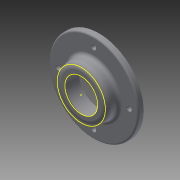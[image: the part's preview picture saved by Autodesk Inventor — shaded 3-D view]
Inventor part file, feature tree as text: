
AUTODESK INVENTOR PART (.ipt)
format: ipt  version: 2014 SP2 (Build 180246200, 246)  size: 164,864 bytes
history: native  units: mm
features: sketch x6, extrude x5, fillet x4, chamfer x1
ambient origin geometry x8: Origin, YZ Plane, XZ Plane, XY Plane, X Axis, Y Axis, Z Axis, Center Point
bodies: Solid1 (feature_tree)
feature tree (16):
  extrude  "Extrusion1"  Depth=28.5mm
  extrude  "Extrusion2"  Depth=13.5mm
  extrude  "Extrusion3"  Depth=3.0mm
  chamfer  "Chamfer2"  Distance=8.0mm
  fillet  "Fillet1"  Radius=50.5mm
  fillet  "Fillet2"  Radius=3.0mm
  fillet  "Fillet3"  Radius=5.0mm
  extrude  "Extrusion4"  Depth=1.0mm
  extrude  "Extrusion5"  Depth=3.0mm
  sketch  "Sketch7"  dims[d21=3.0mm d22=20.0mm d23=3.0mm d24=20.0mm d25=3.0mm d26=20.0mm d27=3.0mm d28=20.0mm d29=11.0mm d30=0.0mm d31=2.5mm d32=0.0mm d33=3.0mm]
  fillet  "Fillet4"  Radius=3.0mm
  sketch  "Sketch1"  dims[d0=22.5mm d1=28.5mm]
  sketch  "Sketch2"  dims[d2=60.0mm d3=13.5mm]
  sketch  "Sketch3"  dims[d4=4.5mm d5=0.0mm d6=22.5mm d7=8.0mm d8=0.0mm d9=50.5mm d10=3.0mm d11=0.0mm]
  sketch  "Sketch5"  dims[d15=4.5mm d16=2.0mm d17=45.0deg d18=5.0mm]
  sketch  "Sketch6"  dims[d19=2.0mm d20=1.0mm]
